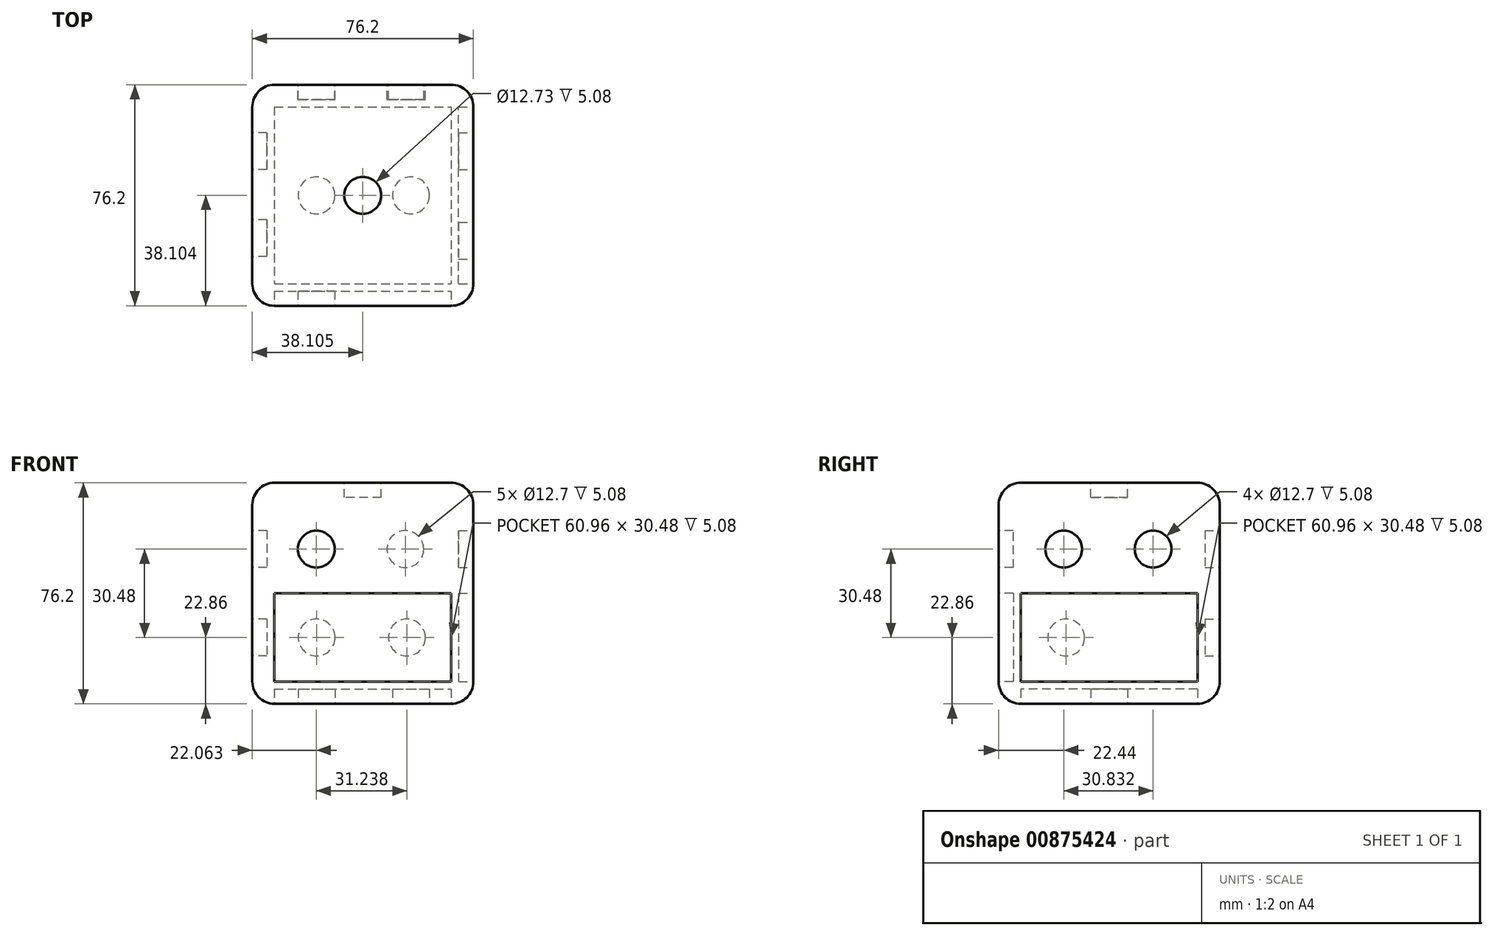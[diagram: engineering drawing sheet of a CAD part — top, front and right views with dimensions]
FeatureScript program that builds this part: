
annotation { "Feature Type Name" : "Feature", "Feature Type Description" : "" }
export const myFeature = defineFeature(function(context is Context, id is Id, definition is map)
    precondition{}
    {
        {
            var Q0;
            Q0=qCreatedBy(makeId("Top.planeOp"),FACE);
            var sketch = newSketch(context, id + "F0", { "sketchPlane" : qUnion([Q0])});
            skLineSegment(sketch, "E0.bottom", {"start": v(-46.22, 31.81) * mm, "end": v(29.98, 31.81) * mm});
            skLineSegment(sketch, "E0.top", {"start": v(-46.22, -44.39) * mm, "end": v(29.98, -44.39) * mm});
            skLineSegment(sketch, "E0.left", {"start": v(-46.22, 31.81) * mm, "end": v(-46.22, -44.39) * mm});
            skLineSegment(sketch, "E0.right", {"start": v(29.98, 31.81) * mm, "end": v(29.98, -44.39) * mm});
            skSolve(sketch);
        }
        {
            var Q0;
            Q0 = qSketchRegion(id + "F0", true);
            extrude(context, id + "F1", {"entities" : qUnion([Q0]), "depth" : 76.2 * mm, "offsetDistance" : 25.4 * mm});
        }
        {
            var Q0;
            Q0=makeQuery(id+"F1.opExtrude","SWEPT_EDGE",EDGE,{"disambiguationData":[OSD([sQuery(id+"F0.wireOp",EDGE,"E0.bottom"),sQuery(id+"F0.wireOp",EDGE,"E0.left")])]});
            var Q1;
            Q1=makeQuery(id+"F1.opExtrude","SWEPT_EDGE",EDGE,{"disambiguationData":[OSD([sQuery(id+"F0.wireOp",EDGE,"E0.bottom"),sQuery(id+"F0.wireOp",EDGE,"E0.right")])]});
            var Q2;
            Q2=makeQuery(id+"F1.opExtrude","SWEPT_EDGE",EDGE,{"disambiguationData":[OSD([sQuery(id+"F0.wireOp",EDGE,"E0.top"),sQuery(id+"F0.wireOp",EDGE,"E0.right")])]});
            var Q3;
            Q3=makeQuery(id+"F1.opExtrude","SWEPT_EDGE",EDGE,{"disambiguationData":[OSD([sQuery(id+"F0.wireOp",EDGE,"E0.top"),sQuery(id+"F0.wireOp",EDGE,"E0.left")])]});
            var Q4;
            Q4=makeQuery(id+"F1.opExtrude","CAP_EDGE",EDGE,{"disambiguationData":[OSD([sQuery(id+"F0.wireOp",EDGE,"E0.bottom")])],"isStart":true});
            var Q5;
            Q5=makeQuery(id+"F1.opExtrude","CAP_EDGE",EDGE,{"disambiguationData":[OSD([sQuery(id+"F0.wireOp",EDGE,"E0.bottom")])],"isStart":false});
            var Q6;
            Q6=makeQuery(id+"F1.opExtrude","CAP_EDGE",EDGE,{"disambiguationData":[OSD([sQuery(id+"F0.wireOp",EDGE,"E0.top")])],"isStart":true});
            var Q7;
            Q7=makeQuery(id+"F1.opExtrude","CAP_EDGE",EDGE,{"disambiguationData":[OSD([sQuery(id+"F0.wireOp",EDGE,"E0.top")])],"isStart":false});
            var Q8;
            Q8=makeQuery(id+"F1.opExtrude","CAP_EDGE",EDGE,{"disambiguationData":[OSD([sQuery(id+"F0.wireOp",EDGE,"E0.right")])],"isStart":true});
            var Q9;
            Q9=makeQuery(id+"F1.opExtrude","CAP_EDGE",EDGE,{"disambiguationData":[OSD([sQuery(id+"F0.wireOp",EDGE,"E0.right")])],"isStart":false});
            var Q10;
            Q10=makeQuery(id+"F1.opExtrude","CAP_EDGE",EDGE,{"disambiguationData":[OSD([sQuery(id+"F0.wireOp",EDGE,"E0.left")])],"isStart":true});
            var Q11;
            Q11=makeQuery(id+"F1.opExtrude","CAP_EDGE",EDGE,{"disambiguationData":[OSD([sQuery(id+"F0.wireOp",EDGE,"E0.left")])],"isStart":false});
            fillet(context, id + "F2", {"entities" : qUnion([Q0, Q1, Q2, Q3, Q4, Q5, Q6, Q7, Q8, Q9, Q10, Q11]), "radius" : 7.62 * mm, "allowEdgeOverflow" : false});
        }
        {
            var Q0;
            Q0=makeQuery(id+"F1.opExtrude","CAP_FACE",FACE,{"disambiguationData":[OSD([sQuery(id+"F0.wireOp",EDGE,"E0.bottom"),sQuery(id+"F0.wireOp",EDGE,"E0.top"),sQuery(id+"F0.wireOp",EDGE,"E0.left"),sQuery(id+"F0.wireOp",EDGE,"E0.right")])],"isStart":false});
            var sketch = newSketch(context, id + "F3", { "sketchPlane" : qUnion([Q0])});
            skLineSegment(sketch, "E1.0", {"start": v(-38.6, 24.2) * mm, "end": v(-38.6, -36.77) * mm});
            skLineSegment(sketch, "E2.0", {"start": v(22.36, 24.2) * mm, "end": v(-38.6, 24.2) * mm});
            skLineSegment(sketch, "E3.0", {"start": v(22.36, -36.77) * mm, "end": v(22.36, 24.2) * mm});
            skLineSegment(sketch, "E4.0", {"start": v(-38.6, -36.77) * mm, "end": v(22.36, -36.77) * mm});
            skLineSegment(sketch, "E5", {"start": v(-8.12, 24.2) * mm, "end": v(-8.12, -36.77) * mm, "construction": true});
            skLineSegment(sketch, "E6", {"start": v(-38.6, -6.29) * mm, "end": v(22.36, -6.29) * mm, "construction": true});
            skCircle(sketch, "E7", {"center": v(-8.12, -6.29) * mm, "radius": 6.36 * mm});
            skSolve(sketch);
        }
        {
            var Q0;
            Q0=makeQuery(id+"F3.imprint","IMPRINT",FACE,{"disambiguationData":[TD([[makeQuery(id+"F3.imprint","IMPRINT",EDGE,{"derivedFrom":sQuery(id+"F3.wireOp",EDGE,"E7")}),1.0]])]});
            var Q1;
            Q1=sQuery(id+"F3.wireOp",EDGE,"E5");
            var Q2;
            Q2=sQuery(id+"F3.wireOp",EDGE,"E6");
            extrude(context, id + "F4", {"entities" : qUnion([Q0]), "operationType" : NewBodyOperationType.REMOVE, "surfaceEntities" : qUnion([Q1, Q2]), "oppositeDirection" : true, "depth" : 5.08 * mm, "offsetDistance" : 25.4 * mm});
        }
        {
            var Q0;
            Q0=makeQuery(id+"F1.opExtrude","CAP_FACE",FACE,{"disambiguationData":[OSD([sQuery(id+"F0.wireOp",EDGE,"E0.bottom"),sQuery(id+"F0.wireOp",EDGE,"E0.top"),sQuery(id+"F0.wireOp",EDGE,"E0.left"),sQuery(id+"F0.wireOp",EDGE,"E0.right")])],"isStart":true});
            var sketch = newSketch(context, id + "F5", { "sketchPlane" : qUnion([Q0])});
            skLineSegment(sketch, "E8.0", {"start": v(-38.6, 36.77) * mm, "end": v(-38.6, -24.2) * mm});
            skLineSegment(sketch, "E9.0", {"start": v(22.36, 36.77) * mm, "end": v(-38.6, 36.77) * mm});
            skLineSegment(sketch, "E10.0", {"start": v(22.36, -24.2) * mm, "end": v(22.36, 36.77) * mm});
            skLineSegment(sketch, "E11.0", {"start": v(-38.6, -24.2) * mm, "end": v(22.36, -24.2) * mm});
            skLineSegment(sketch, "E12", {"start": v(-24.08, 36.77) * mm, "end": v(-24.08, -24.2) * mm});
            skLineSegment(sketch, "E13", {"start": v(8.45, 36.77) * mm, "end": v(8.45, -24.2) * mm});
            skCircle(sketch, "E14", {"center": v(-24.08, 25.34) * mm, "radius": 6.35 * mm});
            skCircle(sketch, "E15", {"center": v(-24.08, 6.29) * mm, "radius": 6.35 * mm});
            skCircle(sketch, "E16", {"center": v(-24.08, -12.76) * mm, "radius": 6.35 * mm});
            skCircle(sketch, "E17", {"center": v(8.45, 25.34) * mm, "radius": 6.35 * mm});
            skCircle(sketch, "E18", {"center": v(8.45, 6.29) * mm, "radius": 6.35 * mm});
            skCircle(sketch, "E19", {"center": v(8.45, -12.76) * mm, "radius": 6.35 * mm});
            skSolve(sketch);
        }
        {
            var Q0;
            {var subQ0=sQuery(id+"F5.wireOp",EDGE,"E15");var subQ1=sQuery(id+"F5.wireOp",EDGE,"E12");var subQ2=makeQuery(id+"F5.imprint","INTERSECT",VERTEX,{"disambiguationData":[OD(0.0)],"derivedFrom":[subQ1,subQ0]});Q0=makeQuery(id+"F5.imprint","IMPRINT",FACE,{"disambiguationData":[TD([[makeQuery(id+"F5.imprint","IMPRINT",EDGE,{"disambiguationData":[TD([[subQ2,-1.0]])],"derivedFrom":subQ1}),1.0]])]});}
            var Q1;
            {var subQ0=sQuery(id+"F5.wireOp",EDGE,"E15");var subQ1=sQuery(id+"F5.wireOp",EDGE,"E12");var subQ2=makeQuery(id+"F5.imprint","INTERSECT",VERTEX,{"disambiguationData":[OD(0.0)],"derivedFrom":[subQ1,subQ0]});Q1=makeQuery(id+"F5.imprint","IMPRINT",FACE,{"disambiguationData":[TD([[makeQuery(id+"F5.imprint","IMPRINT",EDGE,{"disambiguationData":[TD([[subQ2,-1.0]])],"derivedFrom":subQ1}),-1.0]])]});}
            var Q2;
            {var subQ0=sQuery(id+"F5.wireOp",EDGE,"E17");var subQ1=sQuery(id+"F5.wireOp",EDGE,"E13");var subQ2=makeQuery(id+"F5.imprint","INTERSECT",VERTEX,{"disambiguationData":[OD(0.0)],"derivedFrom":[subQ1,subQ0]});Q2=makeQuery(id+"F5.imprint","IMPRINT",FACE,{"disambiguationData":[TD([[makeQuery(id+"F5.imprint","IMPRINT",EDGE,{"disambiguationData":[TD([[subQ2,-1.0]])],"derivedFrom":subQ1}),1.0]])]});}
            var Q3;
            {var subQ0=sQuery(id+"F5.wireOp",EDGE,"E17");var subQ1=sQuery(id+"F5.wireOp",EDGE,"E13");var subQ2=makeQuery(id+"F5.imprint","INTERSECT",VERTEX,{"disambiguationData":[OD(0.0)],"derivedFrom":[subQ1,subQ0]});Q3=makeQuery(id+"F5.imprint","IMPRINT",FACE,{"disambiguationData":[TD([[makeQuery(id+"F5.imprint","IMPRINT",EDGE,{"disambiguationData":[TD([[subQ2,-1.0]])],"derivedFrom":subQ1}),-1.0]])]});}
            var Q4;
            {var subQ0=sQuery(id+"F5.wireOp",EDGE,"E18");var subQ1=sQuery(id+"F5.wireOp",EDGE,"E13");var subQ2=makeQuery(id+"F5.imprint","INTERSECT",VERTEX,{"disambiguationData":[OD(0.0)],"derivedFrom":[subQ1,subQ0]});Q4=makeQuery(id+"F5.imprint","IMPRINT",FACE,{"disambiguationData":[TD([[makeQuery(id+"F5.imprint","IMPRINT",EDGE,{"disambiguationData":[TD([[subQ2,-1.0]])],"derivedFrom":subQ1}),-1.0]])]});}
            var Q5;
            {var subQ0=sQuery(id+"F5.wireOp",EDGE,"E18");var subQ1=sQuery(id+"F5.wireOp",EDGE,"E13");var subQ2=makeQuery(id+"F5.imprint","INTERSECT",VERTEX,{"disambiguationData":[OD(0.0)],"derivedFrom":[subQ1,subQ0]});Q5=makeQuery(id+"F5.imprint","IMPRINT",FACE,{"disambiguationData":[TD([[makeQuery(id+"F5.imprint","IMPRINT",EDGE,{"disambiguationData":[TD([[subQ2,-1.0]])],"derivedFrom":subQ1}),1.0]])]});}
            var Q6;
            {var subQ0=sQuery(id+"F5.wireOp",EDGE,"E14");var subQ1=sQuery(id+"F5.wireOp",EDGE,"E12");var subQ2=makeQuery(id+"F5.imprint","INTERSECT",VERTEX,{"disambiguationData":[OD(0.0)],"derivedFrom":[subQ1,subQ0]});Q6=makeQuery(id+"F5.imprint","IMPRINT",FACE,{"disambiguationData":[TD([[makeQuery(id+"F5.imprint","IMPRINT",EDGE,{"disambiguationData":[TD([[subQ2,-1.0]])],"derivedFrom":subQ1}),-1.0]])]});}
            var Q7;
            {var subQ0=sQuery(id+"F5.wireOp",EDGE,"E19");var subQ1=sQuery(id+"F5.wireOp",EDGE,"E13");var subQ2=makeQuery(id+"F5.imprint","INTERSECT",VERTEX,{"disambiguationData":[OD(0.0)],"derivedFrom":[subQ1,subQ0]});Q7=makeQuery(id+"F5.imprint","IMPRINT",FACE,{"disambiguationData":[TD([[makeQuery(id+"F5.imprint","IMPRINT",EDGE,{"disambiguationData":[TD([[subQ2,-1.0]])],"derivedFrom":subQ1}),-1.0]])]});}
            var Q8;
            {var subQ0=sQuery(id+"F5.wireOp",EDGE,"E19");var subQ1=sQuery(id+"F5.wireOp",EDGE,"E13");var subQ2=makeQuery(id+"F5.imprint","INTERSECT",VERTEX,{"disambiguationData":[OD(0.0)],"derivedFrom":[subQ1,subQ0]});Q8=makeQuery(id+"F5.imprint","IMPRINT",FACE,{"disambiguationData":[TD([[makeQuery(id+"F5.imprint","IMPRINT",EDGE,{"disambiguationData":[TD([[subQ2,-1.0]])],"derivedFrom":subQ1}),1.0]])]});}
            var Q9;
            {var subQ0=sQuery(id+"F5.wireOp",EDGE,"E16");var subQ1=sQuery(id+"F5.wireOp",EDGE,"E12");var subQ2=makeQuery(id+"F5.imprint","INTERSECT",VERTEX,{"disambiguationData":[OD(0.0)],"derivedFrom":[subQ1,subQ0]});Q9=makeQuery(id+"F5.imprint","IMPRINT",FACE,{"disambiguationData":[TD([[makeQuery(id+"F5.imprint","IMPRINT",EDGE,{"disambiguationData":[TD([[subQ2,-1.0]])],"derivedFrom":subQ1}),1.0]])]});}
            var Q10;
            {var subQ0=sQuery(id+"F5.wireOp",EDGE,"E16");var subQ1=sQuery(id+"F5.wireOp",EDGE,"E12");var subQ2=makeQuery(id+"F5.imprint","INTERSECT",VERTEX,{"disambiguationData":[OD(0.0)],"derivedFrom":[subQ1,subQ0]});Q10=makeQuery(id+"F5.imprint","IMPRINT",FACE,{"disambiguationData":[TD([[makeQuery(id+"F5.imprint","IMPRINT",EDGE,{"disambiguationData":[TD([[subQ2,-1.0]])],"derivedFrom":subQ1}),-1.0]])]});}
            var Q11;
            {var subQ0=sQuery(id+"F5.wireOp",EDGE,"E14");var subQ1=sQuery(id+"F5.wireOp",EDGE,"E12");var subQ2=makeQuery(id+"F5.imprint","INTERSECT",VERTEX,{"disambiguationData":[OD(0.0)],"derivedFrom":[subQ1,subQ0]});Q11=makeQuery(id+"F5.imprint","IMPRINT",FACE,{"disambiguationData":[TD([[makeQuery(id+"F5.imprint","IMPRINT",EDGE,{"disambiguationData":[TD([[subQ2,-1.0]])],"derivedFrom":subQ1}),1.0]])]});}
            extrude(context, id + "F6", {"entities" : qUnion([Q0, Q1, Q2, Q3, Q4, Q5, Q6, Q7, Q8, Q9, Q10, Q11]), "operationType" : NewBodyOperationType.REMOVE, "oppositeDirection" : true, "depth" : 5.08 * mm, "offsetDistance" : 25.4 * mm});
        }
        {
            var Q0;
            Q0=makeQuery(id+"F1.opExtrude","SWEPT_FACE",FACE,{"disambiguationData":[OSD([sQuery(id+"F0.wireOp",EDGE,"E0.left")])]});
            extrude(context, id + "F7", {"entities" : qUnion([Q0]), "operationType" : NewBodyOperationType.ADD, "oppositeDirection" : true, "depth" : 5.08 * mm, "offsetDistance" : 25.4 * mm});
        }
        {
            var Q0;
            Q0=makeQuery(id+"F1.opExtrude","SWEPT_FACE",FACE,{"disambiguationData":[OSD([sQuery(id+"F0.wireOp",EDGE,"E0.left")])]});
            var sketch = newSketch(context, id + "F8", { "sketchPlane" : qUnion([Q0])});
            skSolve(sketch);
        }
        {
            var Q0;
            {var subQ0=sQuery(id+"F0.wireOp",EDGE,"E0.left");var subQ1=makeQuery(id+"F1.opExtrude","SWEPT_FACE",FACE,{"disambiguationData":[OSD([subQ0])]});Q0=makeQuery(id+"F8.imprint","IMPRINT",FACE,{"disambiguationData":[TD([[makeQuery(id+"F8.imprint","IMPRINT",EDGE,{"derivedFrom":makeQuery(id+"F2.opFillet","BLEND_EDGE",EDGE,{"blendedFrom":[makeQuery(id+"F1.opExtrude","CAP_EDGE",EDGE,{"disambiguationData":[OSD([subQ0])],"isStart":true}),subQ1],"blendedInto":[subQ1]})}),1.0]])]});}
            var sketch = newSketch(context, id + "F9", { "sketchPlane" : qUnion([Q0])});
            skLineSegment(sketch, "E20.0", {"start": v(36.77, 68.58) * mm, "end": v(-24.2, 68.58) * mm});
            skLineSegment(sketch, "E21.0", {"start": v(36.77, 7.62) * mm, "end": v(36.77, 68.58) * mm});
            skLineSegment(sketch, "E22.0.1", {"start": v(-24.2, 68.58) * mm, "end": v(-24.2, 7.62) * mm});
            skLineSegment(sketch, "E22.0.2", {"start": v(-24.2, 7.62) * mm, "end": v(36.77, 7.62) * mm});
            skLineSegment(sketch, "E23", {"start": v(6.29, 68.58) * mm, "end": v(6.29, 7.62) * mm});
            skLineSegment(sketch, "E24", {"start": v(-24.2, 38.1) * mm, "end": v(36.77, 38.1) * mm});
            skCircle(sketch, "E25", {"center": v(-8.88, 53.34) * mm, "radius": 6.35 * mm});
            skCircle(sketch, "E26", {"center": v(21.08, 22.86) * mm, "radius": 6.35 * mm});
            skSolve(sketch);
        }
        {
            var Q0;
            Q0=makeQuery(id+"F9.imprint","IMPRINT",FACE,{"disambiguationData":[TD([[makeQuery(id+"F9.imprint","IMPRINT",EDGE,{"derivedFrom":sQuery(id+"F9.wireOp",EDGE,"E25")}),1.0]])]});
            var Q1;
            Q1=makeQuery(id+"F9.imprint","IMPRINT",FACE,{"disambiguationData":[TD([[makeQuery(id+"F9.imprint","IMPRINT",EDGE,{"derivedFrom":sQuery(id+"F9.wireOp",EDGE,"E26")}),1.0]])]});
            extrude(context, id + "F10", {"entities" : qUnion([Q0, Q1]), "operationType" : NewBodyOperationType.REMOVE, "oppositeDirection" : true, "depth" : 5.08 * mm, "offsetDistance" : 25.4 * mm});
        }
        {
            var Q0;
            Q0=makeQuery(id+"F1.opExtrude","SWEPT_FACE",FACE,{"disambiguationData":[OSD([sQuery(id+"F0.wireOp",EDGE,"E0.right")])]});
            var sketch = newSketch(context, id + "F11", { "sketchPlane" : qUnion([Q0])});
            skLineSegment(sketch, "E27.0", {"start": v(24.2, 68.58) * mm, "end": v(-36.77, 68.58) * mm});
            skLineSegment(sketch, "E28.0", {"start": v(-36.77, 68.58) * mm, "end": v(-36.77, 7.62) * mm});
            skLineSegment(sketch, "E29.0", {"start": v(24.2, 7.62) * mm, "end": v(24.2, 68.58) * mm});
            skLineSegment(sketch, "E30", {"start": v(-6.29, 68.58) * mm, "end": v(-6.29, 7.62) * mm});
            skLineSegment(sketch, "E31", {"start": v(-36.77, 38.1) * mm, "end": v(24.2, 38.1) * mm});
            skCircle(sketch, "E32", {"center": v(-21.95, 53.34) * mm, "radius": 6.35 * mm});
            skCircle(sketch, "E33", {"center": v(8.88, 53.34) * mm, "radius": 6.35 * mm});
            skCircle(sketch, "E34", {"center": v(9.5, 22.86) * mm, "radius": 6.35 * mm});
            skCircle(sketch, "E35", {"center": v(-21.95, 22.86) * mm, "radius": 6.35 * mm});
            skCircle(sketch, "E36", {"center": v(-6.29, 38.1) * mm, "radius": 6.35 * mm});
            skSolve(sketch);
        }
        {
            var Q0;
            Q0=makeQuery(id+"F11.imprint","IMPRINT",FACE,{"disambiguationData":[TD([[makeQuery(id+"F11.imprint","IMPRINT",EDGE,{"derivedFrom":sQuery(id+"F11.wireOp",EDGE,"E32")}),1.0]])]});
            var Q1;
            {var subQ0=sQuery(id+"F11.wireOp",EDGE,"E36");var subQ1=sQuery(id+"F11.wireOp",EDGE,"E30");var subQ2=makeQuery(id+"F11.imprint","INTERSECT",VERTEX,{"disambiguationData":[OD(0.0)],"derivedFrom":[subQ1,subQ0]});Q1=makeQuery(id+"F11.imprint","IMPRINT",FACE,{"disambiguationData":[TD([[makeQuery(id+"F11.imprint","IMPRINT",EDGE,{"disambiguationData":[TD([[subQ2,-1.0]])],"derivedFrom":subQ1}),1.0]])]});}
            var Q2;
            {var subQ0=sQuery(id+"F11.wireOp",EDGE,"E31");var subQ1=sQuery(id+"F11.wireOp",EDGE,"E30");var subQ2=makeQuery(id+"F11.imprint","INTERSECT",VERTEX,{"derivedFrom":[subQ1,subQ0]});Q2=makeQuery(id+"F11.imprint","IMPRINT",FACE,{"disambiguationData":[TD([[makeQuery(id+"F11.imprint","IMPRINT",EDGE,{"disambiguationData":[TD([[subQ2,-1.0]])],"derivedFrom":subQ1}),1.0]])]});}
            var Q3;
            {var subQ0=sQuery(id+"F11.wireOp",EDGE,"E31");var subQ1=sQuery(id+"F11.wireOp",EDGE,"E30");var subQ2=makeQuery(id+"F11.imprint","INTERSECT",VERTEX,{"derivedFrom":[subQ1,subQ0]});Q3=makeQuery(id+"F11.imprint","IMPRINT",FACE,{"disambiguationData":[TD([[makeQuery(id+"F11.imprint","IMPRINT",EDGE,{"disambiguationData":[TD([[subQ2,-1.0]])],"derivedFrom":subQ1}),-1.0]])]});}
            var Q4;
            {var subQ0=sQuery(id+"F11.wireOp",EDGE,"E36");var subQ1=sQuery(id+"F11.wireOp",EDGE,"E30");var subQ2=makeQuery(id+"F11.imprint","INTERSECT",VERTEX,{"disambiguationData":[OD(0.0)],"derivedFrom":[subQ1,subQ0]});Q4=makeQuery(id+"F11.imprint","IMPRINT",FACE,{"disambiguationData":[TD([[makeQuery(id+"F11.imprint","IMPRINT",EDGE,{"disambiguationData":[TD([[subQ2,-1.0]])],"derivedFrom":subQ1}),-1.0]])]});}
            var Q5;
            Q5=makeQuery(id+"F11.imprint","IMPRINT",FACE,{"disambiguationData":[TD([[makeQuery(id+"F11.imprint","IMPRINT",EDGE,{"derivedFrom":sQuery(id+"F11.wireOp",EDGE,"E33")}),1.0]])]});
            var Q6;
            Q6=makeQuery(id+"F11.imprint","IMPRINT",FACE,{"disambiguationData":[TD([[makeQuery(id+"F11.imprint","IMPRINT",EDGE,{"derivedFrom":sQuery(id+"F11.wireOp",EDGE,"E34")}),1.0]])]});
            var Q7;
            Q7=makeQuery(id+"F11.imprint","IMPRINT",FACE,{"disambiguationData":[TD([[makeQuery(id+"F11.imprint","IMPRINT",EDGE,{"derivedFrom":sQuery(id+"F11.wireOp",EDGE,"E35")}),1.0]])]});
            extrude(context, id + "F12", {"entities" : qUnion([Q0, Q1, Q2, Q3, Q4, Q5, Q6, Q7]), "operationType" : NewBodyOperationType.REMOVE, "oppositeDirection" : true, "depth" : 5.08 * mm, "offsetDistance" : 25.4 * mm});
        }
        {
            var Q0;
            Q0=makeQuery(id+"F1.opExtrude","SWEPT_FACE",FACE,{"disambiguationData":[OSD([sQuery(id+"F0.wireOp",EDGE,"E0.top")])]});
            var sketch = newSketch(context, id + "F13", { "sketchPlane" : qUnion([Q0])});
            skLineSegment(sketch, "E37.0", {"start": v(22.36, 68.58) * mm, "end": v(-38.6, 68.58) * mm});
            skLineSegment(sketch, "E38.0", {"start": v(-38.6, 68.58) * mm, "end": v(-38.6, 7.62) * mm});
            skLineSegment(sketch, "E39.0", {"start": v(22.36, 7.62) * mm, "end": v(22.36, 68.58) * mm});
            skLineSegment(sketch, "E40.0", {"start": v(-38.6, 7.62) * mm, "end": v(22.36, 7.62) * mm});
            skLineSegment(sketch, "E41", {"start": v(-8.12, 68.58) * mm, "end": v(-8.12, 7.62) * mm});
            skLineSegment(sketch, "E42", {"start": v(-38.6, 38.1) * mm, "end": v(22.36, 38.1) * mm});
            skCircle(sketch, "E43", {"center": v(-8.12, 38.1) * mm, "radius": 6.35 * mm});
            skCircle(sketch, "E44", {"center": v(-24.14, 53.34) * mm, "radius": 6.35 * mm});
            skCircle(sketch, "E45", {"center": v(7.03, 22.86) * mm, "radius": 6.35 * mm});
            skSolve(sketch);
        }
        {
            var Q0;
            Q0=makeQuery(id+"F13.imprint","IMPRINT",FACE,{"disambiguationData":[TD([[makeQuery(id+"F13.imprint","IMPRINT",EDGE,{"derivedFrom":sQuery(id+"F13.wireOp",EDGE,"E44")}),1.0]])]});
            var Q1;
            {var subQ0=sQuery(id+"F13.wireOp",EDGE,"E43");var subQ1=sQuery(id+"F13.wireOp",EDGE,"E41");var subQ2=makeQuery(id+"F13.imprint","INTERSECT",VERTEX,{"disambiguationData":[OD(0.0)],"derivedFrom":[subQ1,subQ0]});Q1=makeQuery(id+"F13.imprint","IMPRINT",FACE,{"disambiguationData":[TD([[makeQuery(id+"F13.imprint","IMPRINT",EDGE,{"disambiguationData":[TD([[subQ2,-1.0]])],"derivedFrom":subQ1}),1.0]])]});}
            var Q2;
            {var subQ0=sQuery(id+"F13.wireOp",EDGE,"E42");var subQ1=sQuery(id+"F13.wireOp",EDGE,"E41");var subQ2=makeQuery(id+"F13.imprint","INTERSECT",VERTEX,{"derivedFrom":[subQ1,subQ0]});Q2=makeQuery(id+"F13.imprint","IMPRINT",FACE,{"disambiguationData":[TD([[makeQuery(id+"F13.imprint","IMPRINT",EDGE,{"disambiguationData":[TD([[subQ2,-1.0]])],"derivedFrom":subQ1}),1.0]])]});}
            var Q3;
            {var subQ0=sQuery(id+"F13.wireOp",EDGE,"E42");var subQ1=sQuery(id+"F13.wireOp",EDGE,"E41");var subQ2=makeQuery(id+"F13.imprint","INTERSECT",VERTEX,{"derivedFrom":[subQ1,subQ0]});Q3=makeQuery(id+"F13.imprint","IMPRINT",FACE,{"disambiguationData":[TD([[makeQuery(id+"F13.imprint","IMPRINT",EDGE,{"disambiguationData":[TD([[subQ2,-1.0]])],"derivedFrom":subQ1}),-1.0]])]});}
            var Q4;
            {var subQ0=sQuery(id+"F13.wireOp",EDGE,"E43");var subQ1=sQuery(id+"F13.wireOp",EDGE,"E41");var subQ2=makeQuery(id+"F13.imprint","INTERSECT",VERTEX,{"disambiguationData":[OD(0.0)],"derivedFrom":[subQ1,subQ0]});Q4=makeQuery(id+"F13.imprint","IMPRINT",FACE,{"disambiguationData":[TD([[makeQuery(id+"F13.imprint","IMPRINT",EDGE,{"disambiguationData":[TD([[subQ2,-1.0]])],"derivedFrom":subQ1}),-1.0]])]});}
            var Q5;
            Q5=makeQuery(id+"F13.imprint","IMPRINT",FACE,{"disambiguationData":[TD([[makeQuery(id+"F13.imprint","IMPRINT",EDGE,{"derivedFrom":sQuery(id+"F13.wireOp",EDGE,"E45")}),1.0]])]});
            extrude(context, id + "F14", {"entities" : qUnion([Q0, Q1, Q2, Q3, Q4, Q5]), "operationType" : NewBodyOperationType.REMOVE, "oppositeDirection" : true, "depth" : 5.08 * mm, "offsetDistance" : 25.4 * mm});
        }
        {
            var Q0;
            Q0=makeQuery(id+"F1.opExtrude","SWEPT_FACE",FACE,{"disambiguationData":[OSD([sQuery(id+"F0.wireOp",EDGE,"E0.bottom")])]});
            var sketch = newSketch(context, id + "F15", { "sketchPlane" : qUnion([Q0])});
            skLineSegment(sketch, "E46.0", {"start": v(-22.36, 7.62) * mm, "end": v(38.6, 7.62) * mm});
            skLineSegment(sketch, "E47.0", {"start": v(38.6, 7.62) * mm, "end": v(38.6, 68.58) * mm});
            skLineSegment(sketch, "E48.0", {"start": v(-22.36, 68.58) * mm, "end": v(-22.36, 7.62) * mm});
            skLineSegment(sketch, "E49.0", {"start": v(38.6, 68.58) * mm, "end": v(-22.36, 68.58) * mm});
            skLineSegment(sketch, "E50", {"start": v(8.12, 7.62) * mm, "end": v(8.12, 68.58) * mm});
            skLineSegment(sketch, "E51", {"start": v(38.6, 38.1) * mm, "end": v(-22.36, 38.1) * mm});
            skCircle(sketch, "E52", {"center": v(24.03, 22.86) * mm, "radius": 6.35 * mm});
            skCircle(sketch, "E53", {"center": v(-7.08, 22.86) * mm, "radius": 6.35 * mm});
            skCircle(sketch, "E54", {"center": v(-6.52, 53.34) * mm, "radius": 6.35 * mm});
            skCircle(sketch, "E55", {"center": v(24.16, 53.34) * mm, "radius": 6.35 * mm});
            skSolve(sketch);
        }
        {
            var Q0;
            Q0=makeQuery(id+"F15.imprint","IMPRINT",FACE,{"disambiguationData":[TD([[makeQuery(id+"F15.imprint","IMPRINT",EDGE,{"derivedFrom":sQuery(id+"F15.wireOp",EDGE,"E52")}),1.0]])]});
            var Q1;
            Q1=makeQuery(id+"F15.imprint","IMPRINT",FACE,{"disambiguationData":[TD([[makeQuery(id+"F15.imprint","IMPRINT",EDGE,{"derivedFrom":sQuery(id+"F15.wireOp",EDGE,"E55")}),1.0]])]});
            var Q2;
            Q2=makeQuery(id+"F15.imprint","IMPRINT",FACE,{"disambiguationData":[TD([[makeQuery(id+"F15.imprint","IMPRINT",EDGE,{"derivedFrom":sQuery(id+"F15.wireOp",EDGE,"E54")}),1.0]])]});
            var Q3;
            Q3=makeQuery(id+"F15.imprint","IMPRINT",FACE,{"disambiguationData":[TD([[makeQuery(id+"F15.imprint","IMPRINT",EDGE,{"derivedFrom":sQuery(id+"F15.wireOp",EDGE,"E53")}),1.0]])]});
            extrude(context, id + "F16", {"entities" : qUnion([Q0, Q1, Q2, Q3]), "operationType" : NewBodyOperationType.REMOVE, "oppositeDirection" : true, "depth" : 5.08 * mm, "offsetDistance" : 25.4 * mm});
        }
    });
